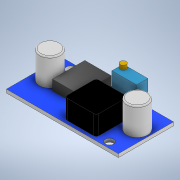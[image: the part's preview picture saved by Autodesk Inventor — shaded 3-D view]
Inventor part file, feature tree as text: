
AUTODESK INVENTOR PART (.ipt)
format: ipt  version: 2022 (Build 260153000, 153)  size: 217,088 bytes
history: native  units: in
note: dims shown in document units (in); Inventor stores cm internally (conversion verified against a paired STEP export)
features: extrude x7, sketch x7, fillet x1
ambient origin geometry x8: Origin, YZ Plane, XZ Plane, XY Plane, X Axis, Y Axis, Z Axis, Center Point
bodies: Solid1 (feature_tree)
feature tree (15):
  extrude  "Extrusion1"  Depth=0.8346in
  extrude  "Extrusion2"  Depth=0.8465in
  extrude  "Extrusion3"  Depth=0.4882in
  extrude  "Extrusion4"  Depth=0.3228in
  extrude  "Extrusion5"  Depth=0.1575in TaperAngle=0.0deg
  extrude  "Extrusion6"  Depth=0.4803in
  fillet  "Fillet1"  Radius=0.0472in
  extrude  "Extrusion7"  Depth=0.0394in
  sketch  "Sketch1"  dims[d0=1.6929in d1=0.8346in]
  sketch  "Sketch2"  dims[d2=0.4173in d3=0.8465in]
  sketch  "Sketch3"  dims[d4=0.0516in d5=0.0in d6=0.4882in]
  sketch  "Sketch4"  dims[d7=0.3996in d8=0.3228in]
  sketch  "Sketch5"  dims[d9=0.374in d10=0.1575in d11=0.0in]
  sketch  "Sketch6"  dims[d12=0.4803in d13=0.4803in d14=0.0472in]
  sketch  "Sketch7"  dims[d15=0.3819in d16=0.0394in d17=0.2913in d18=0.0in d19=0.1697in d20=0.3728in d21=0.3689in d22=0.0197in d23=0.3937in d24=0.0in d25=0.0886in d26=0.0472in d27=0.0472in d28=0.0634in d29=0.0in d30=0.315in d31=0.315in d32=0.4657in d33=0.1799in d34=0.2055in d35=0.4516in d36=0.4134in d37=0.0in d38=0.0197in d39=0.1252in d42=0.1252in d43=0.2252in d44=0.0906in d45=0.0906in d46=0.2252in d47=0.1252in d48=0.0in]
